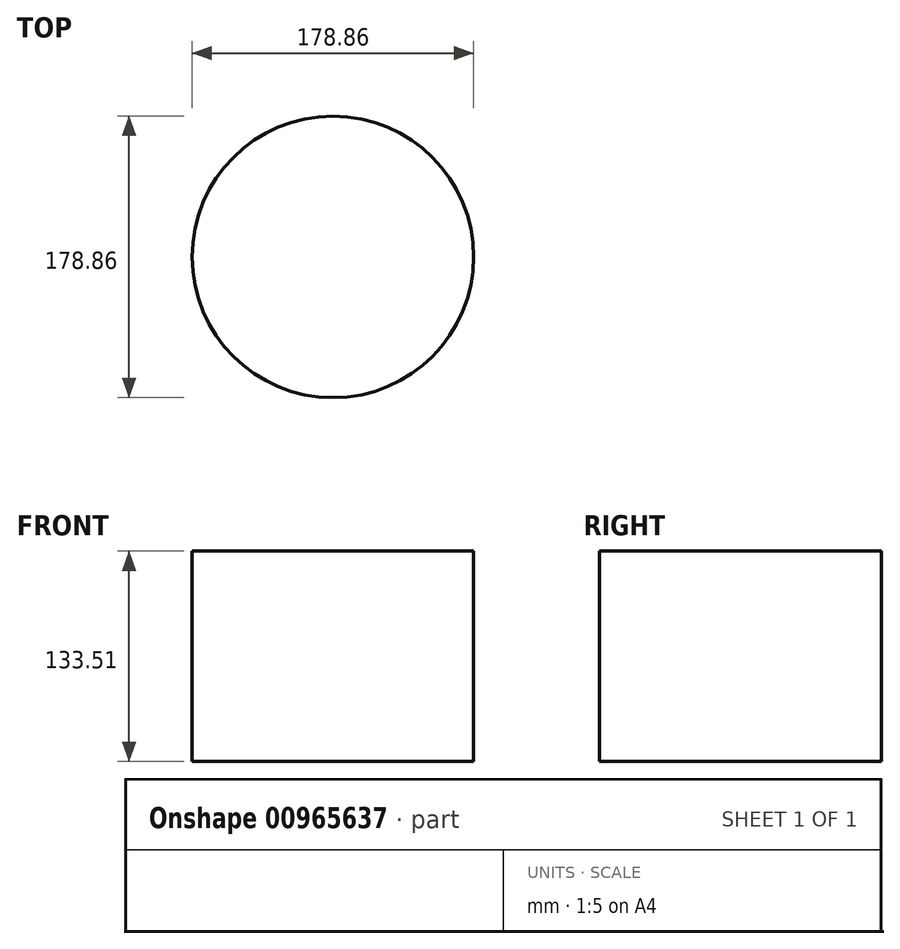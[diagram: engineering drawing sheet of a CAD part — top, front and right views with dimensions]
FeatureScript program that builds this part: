
annotation { "Feature Type Name" : "Feature", "Feature Type Description" : "" }
export const myFeature = defineFeature(function(context is Context, id is Id, definition is map)
    precondition{}
    {
        {
            var Q0;
            Q0=qCreatedBy(makeId("Front.planeOp"),FACE);
            var sketch = newSketch(context, id + "F0", { "sketchPlane" : qUnion([Q0])});
            skLineSegment(sketch, "E0", {"start": v(89.43, 0) * mm, "end": v(0, 0) * mm});
            skLineSegment(sketch, "E1", {"start": v(89.43, 0) * mm, "end": v(89.43, 133.51) * mm});
            skLineSegment(sketch, "E2", {"start": v(89.43, 133.51) * mm, "end": v(0, 133.51) * mm});
            skLineSegment(sketch, "E3", {"start": v(0, 133.51) * mm, "end": v(0, 0) * mm});
            skSolve(sketch);
        }
        {
            var Q0;
            Q0=makeQuery(id+"F0.imprint","IMPRINT",FACE,{"disambiguationData":[TD([[makeQuery(id+"F0.imprint","IMPRINT",EDGE,{"derivedFrom":sQuery(id+"F0.wireOp",EDGE,"E0")}),-1.0]])]});
            var sketch = newSketch(context, id + "F1", { "sketchPlane" : qUnion([Q0])});
            skLineSegment(sketch, "E4", {"start": v(-28.15, 0) * mm, "end": v(-28.15, 146.15) * mm});
            skSolve(sketch);
        }
        {
            var Q0;
            Q0=makeQuery(id+"F1.imprint","IMPRINT",FACE,{"disambiguationData":[TD([[makeQuery(id+"F1.imprint","IMPRINT",EDGE,{"derivedFrom":makeQuery(id+"F0.imprint","IMPRINT",EDGE,{"derivedFrom":sQuery(id+"F0.wireOp",EDGE,"E0")})}),-1.0]])]});
            var Q1;
            Q1=makeQuery(id+"F0.imprint","IMPRINT",FACE,{"disambiguationData":[TD([[makeQuery(id+"F0.imprint","IMPRINT",EDGE,{"derivedFrom":sQuery(id+"F0.wireOp",EDGE,"E0")}),-1.0]])]});
            var Q2;
            Q2=sQuery(id+"F1.wireOp",EDGE,"E4");
            var Q3;
            Q3=sQuery(id+"F0.wireOp",EDGE,"E3");
            revolve(context, id + "F2", {"surfaceOperationType" : NewSurfaceOperationType.NEW, "entities" : qUnion([Q0, Q1]), "surfaceEntities" : qUnion([Q2]), "axis" : qUnion([Q3]), "revolveType" : RevolveType.FULL});
        }
    });
